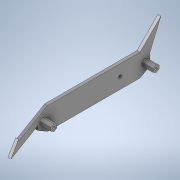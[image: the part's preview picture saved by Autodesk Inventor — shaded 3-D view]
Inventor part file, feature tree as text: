
AUTODESK INVENTOR PART (.ipt)
format: ipt  version: 2020 (Build 240168000, 168)  size: 180,224 bytes
history: native  units: in
note: dims shown in document units (in); Inventor stores cm internally (conversion verified against a paired STEP export)
features: other x3, extrude x2, sketch x2
ambient origin geometry x8: Origin, YZ Plane, XZ Plane, XY Plane, X Axis, Y Axis, Z Axis, Center Point
bodies: Solid1 (feature_tree)
feature tree (7):
  other  "HexWheelGuard.ipt"
  extrude  "Extrusion1"  TaperAngle=0.0deg  [1 undecoded]
  extrude  "Extrusion2"  Depth=0.5906in
  other  "Solid1::HexWheelGuard.ipt"
  other  "TaggingFeature1"
  sketch  "Sketch1"  dims[d0=0.3937in d6=0.0in d7=0.0in]
  sketch  "Sketch2"  dims[d9=0.315in d10=1.4843in d11=60.0deg d12=0.0787in d13=0.3937in d14=0.0in d20=0.3937in d21=0.5906in d22=1.1024in]
note: 1 required parameter value undecoded (feature->parameter linkage not recoverable at this tier; creation-order binding heuristic only, values carry confidence <= 0.55)
